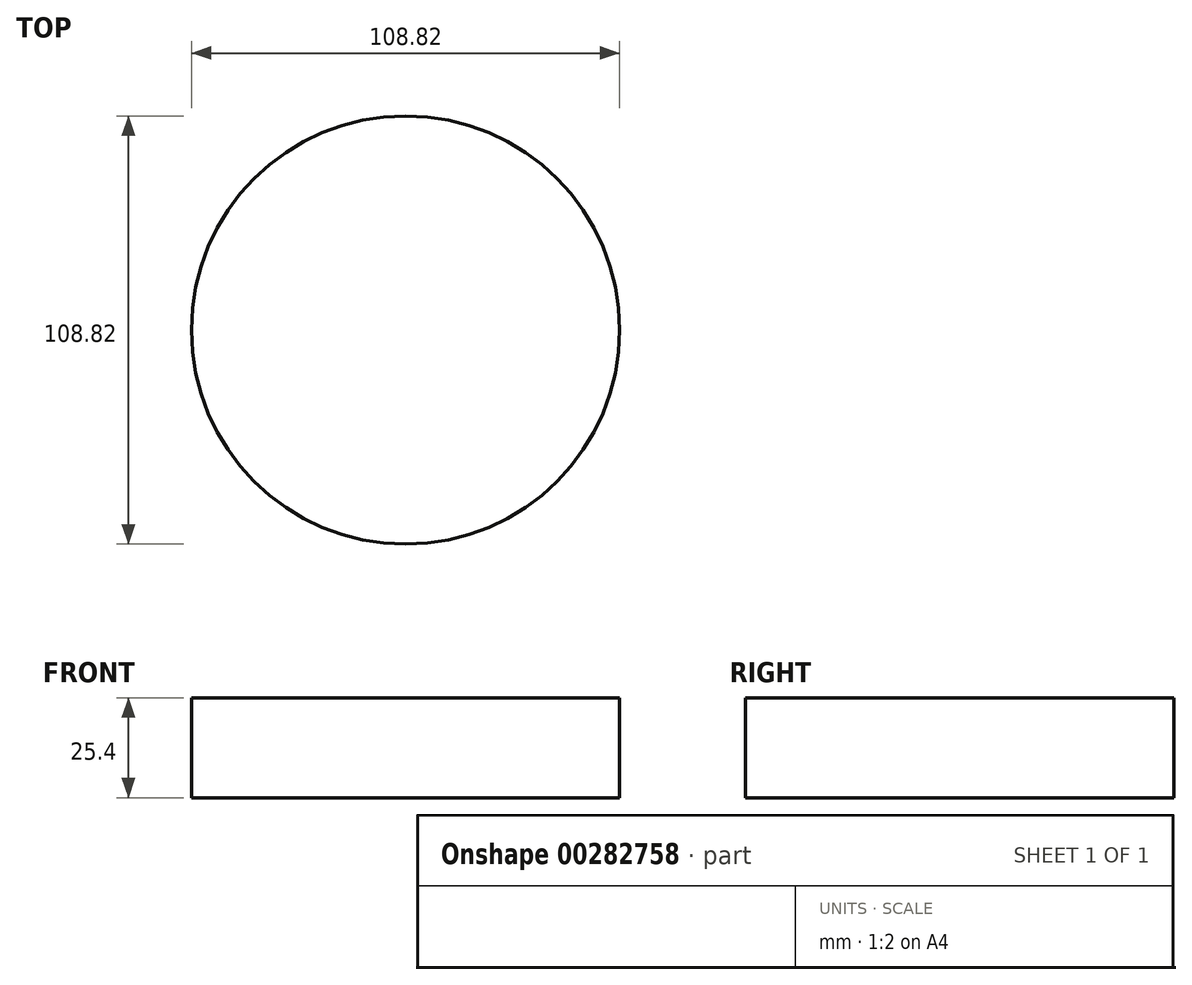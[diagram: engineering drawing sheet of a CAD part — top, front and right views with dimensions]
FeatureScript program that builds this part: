
annotation { "Feature Type Name" : "Feature", "Feature Type Description" : "" }
export const myFeature = defineFeature(function(context is Context, id is Id, definition is map)
    precondition{}
    {
        {
            var Q0;
            Q0=qCreatedBy(makeId("Top.planeOp"),FACE);
            var sketch = newSketch(context, id + "F0", { "sketchPlane" : qUnion([Q0])});
            skCircle(sketch, "E0", {"center": v(0, 0) * mm, "radius": 54.4 * mm});
            skSolve(sketch);
        }
        {
            var Q0;
            Q0=makeQuery(id+"F0.imprint","IMPRINT",FACE,{"disambiguationData":[TD([[makeQuery(id+"F0.imprint","IMPRINT",EDGE,{"derivedFrom":sQuery(id+"F0.wireOp",EDGE,"E0")}),1.0]])]});
            extrude(context, id + "F1", {"entities" : qUnion([Q0]), "depth" : 25.4 * mm});
        }
    });
